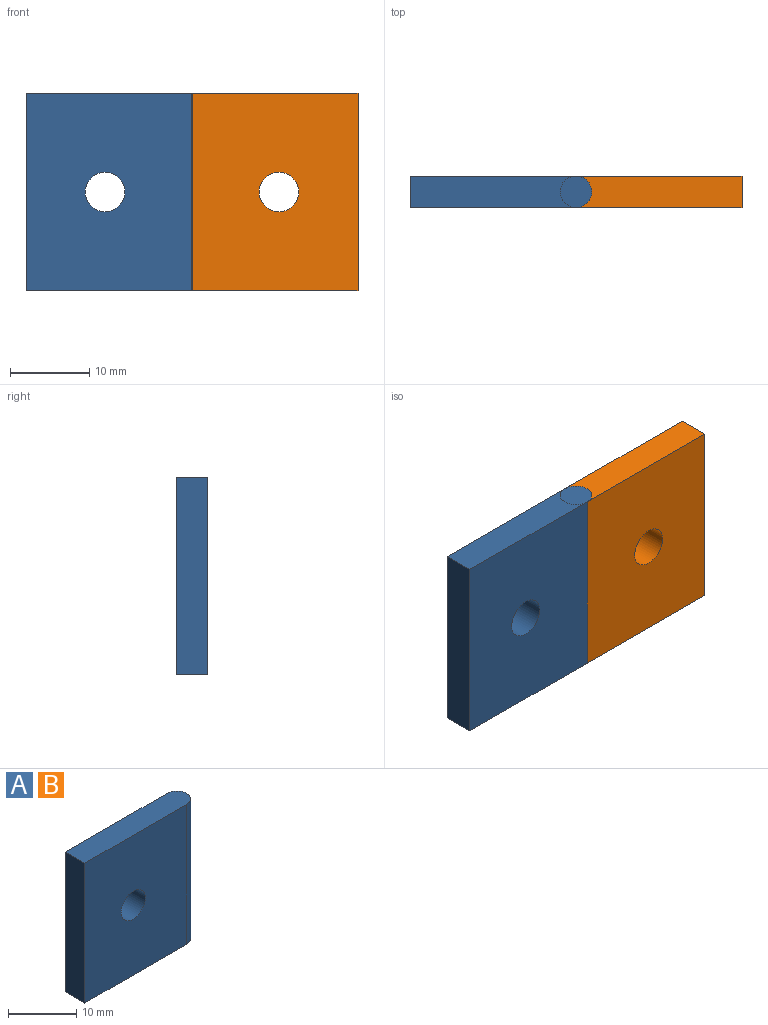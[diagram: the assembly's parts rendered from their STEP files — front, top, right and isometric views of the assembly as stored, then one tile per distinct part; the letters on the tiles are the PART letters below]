
ASSEMBLY  parts=2 mates=1
PART A: 7 faces, bbox 23x4x25 mm
  f0: plane 25x21mm, normal (0,1,0), area 505.4mm2, adj f1,f3,f4,f5,f6
  f1: plane 25x4mm, normal (-1,0,0), area 100mm2, adj f0,f2,f4,f5
  f2: plane 25x21mm, normal (0,-1,0), area 505.4mm2, adj f1,f3,f4,f5,f6
  f3: cylinder r=2mm len=25mm, axis (0,0,-1), area 157.1mm2, adj f0,f2,f4,f5
  f4: plane 23x4mm, normal (0,0,1), area 90.3mm2, adj f0,f1,f2,f3
  f5: plane 23x4mm, normal (0,0,-1), area 90.3mm2, adj f0,f1,f2,f3
  f6: cylinder r=2.5mm len=5mm, axis (0,1,0), area 62.8mm2, adj f0,f2
PART B: same geometry as A
PLACE A rot(axis=(-1,0,0),0deg) t=(22.58,21.81,3.41)mm
PLACE B rot(axis=(0,0,1),180deg) t=(-225.84,-166.7,3.41)mm
MATE revolute A.f3 <-> B.f3  axis (0,0,1) through (-101.63,-72.45,28.41)mm
